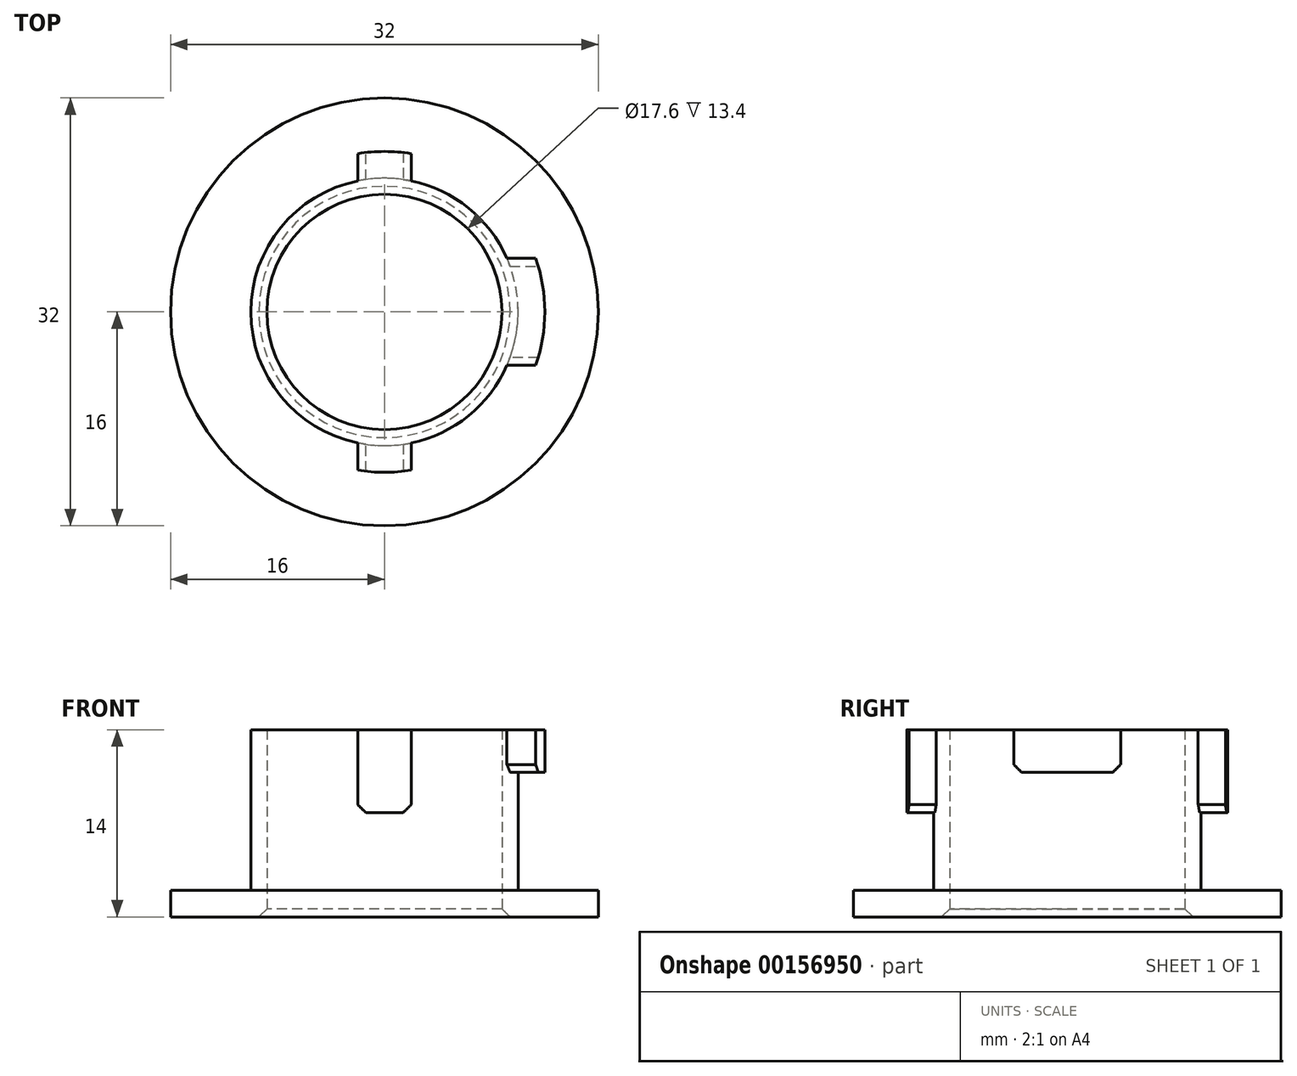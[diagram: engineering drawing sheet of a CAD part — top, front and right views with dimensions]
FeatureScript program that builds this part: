
annotation { "Feature Type Name" : "Feature", "Feature Type Description" : "" }
export const myFeature = defineFeature(function(context is Context, id is Id, definition is map)
    precondition{}
    {
        {
            var Q0;
            Q0=qCreatedBy(makeId("Top.planeOp"),FACE);
            var sketch = newSketch(context, id + "F0", { "sketchPlane" : qUnion([Q0])});
            skCircle(sketch, "E0", {"center": v(0, 0) * mm, "radius": 16 * mm});
            skCircle(sketch, "E1", {"center": v(0, 0) * mm, "radius": 8.8 * mm});
            skSolve(sketch);
        }
        {
            var Q0;
            Q0 = qSketchRegion(id + "F0", true);
            extrude(context, id + "F1", {"entities" : qUnion([Q0]), "depth" : 2 * mm});
        }
        {
            var Q0;
            Q0=makeQuery(id+"F1.opExtrude","CAP_FACE",FACE,{"disambiguationData":[OSD([sQuery(id+"F0.wireOp",EDGE,"E0"),sQuery(id+"F0.wireOp",EDGE,"E1")])],"isStart":false});
            var sketch = newSketch(context, id + "F2", { "sketchPlane" : qUnion([Q0])});
            skCircle(sketch, "E2", {"center": v(0, 0) * mm, "radius": 10 * mm});
            skSolve(sketch);
        }
        {
            var Q0;
            Q0=makeQuery(id+"F2.imprint","IMPRINT",FACE,{"disambiguationData":[TD([[makeQuery(id+"F2.imprint","IMPRINT",EDGE,{"derivedFrom":sQuery(id+"F2.wireOp",EDGE,"E2")}),1.0]])]});
            extrude(context, id + "F3", {"entities" : qUnion([Q0]), "operationType" : NewBodyOperationType.ADD, "depth" : 12 * mm});
        }
        {
            var Q0;
            Q0=makeQuery(id+"F1.opExtrude","CAP_FACE",FACE,{"disambiguationData":[OSD([sQuery(id+"F0.wireOp",EDGE,"E0"),sQuery(id+"F0.wireOp",EDGE,"E1")])],"isStart":false});
            cPlane(context, id + "F4", {"entities" : qUnion([Q0]), "cplaneType" : CPlaneType.OFFSET, "offset" : (3.8 + 2) * mm, "width" : 150 * mm, "height" : 150 * mm});
        }
        {
            var Q0;
            Q0=qCreatedBy(id+"F4.planeOp",FACE);
            var sketch = newSketch(context, id + "F5", { "sketchPlane" : qUnion([Q0])});
            skLineSegment(sketch, "E3", {"start": v(-2, -11.83) * mm, "end": v(-2, -9.8) * mm});
            skArc(sketch, "E4.0", {"start": v(-2, -9.8) * mm, "mid": v(0, -10) * mm, "end": v(2, -9.8) * mm});
            skLineSegment(sketch, "E5.MirrorCS", {"start": v(2, -11.83) * mm, "end": v(2, -9.8) * mm});
            skLineSegment(sketch, "E6.MirrorCS", {"start": v(-2, 11.83) * mm, "end": v(-2, 9.8) * mm});
            skLineSegment(sketch, "E7.MirrorCS", {"start": v(2, 11.83) * mm, "end": v(2, 9.8) * mm});
            skArc(sketch, "E8.trimOffspring", {"start": v(2, 9.8) * mm, "mid": v(0, 10) * mm, "end": v(-2, 9.8) * mm});
            skPoint(sketch, "E9.orphan", {"position": v(12, -4) * mm});
            skPoint(sketch, "E10.MirrorCS.end.orphan", {"position": v(12, 0) * mm});
            skPoint(sketch, "E10.MirrorCS.start.orphan", {"position": v(12, 4) * mm});
            skArc(sketch, "E11.trimOffspring", {"start": v(-2, -11.83) * mm, "mid": v(0, -12) * mm, "end": v(2, -11.83) * mm});
            skPoint(sketch, "E12.end.orphan", {"position": v(0, -12) * mm});
            skPoint(sketch, "E13.MirrorCS.start.orphan", {"position": v(2, -12) * mm});
            skPoint(sketch, "E14.orphan", {"position": v(-2, -12) * mm});
            skArc(sketch, "E15.trimOffspring", {"start": v(2, 11.83) * mm, "mid": v(0, 12) * mm, "end": v(-2, 11.83) * mm});
            skPoint(sketch, "E16.MirrorCS.end.orphan", {"position": v(0, 12) * mm});
            skPoint(sketch, "E16.MirrorCS.start.orphan", {"position": v(-2, 12) * mm});
            skPoint(sketch, "E17.MirrorCS.start.orphan", {"position": v(2, 12) * mm});
            skSolve(sketch);
        }
        {
            var Q0;
            Q0 = qSketchRegion(id + "F5", true);
            var Q1;
            Q1=makeQuery(id+"F3.opExtrude","CAP_FACE",FACE,{"disambiguationData":[OSD([sQuery(id+"F0.wireOp",EDGE,"E1"),sQuery(id+"F2.wireOp",EDGE,"E2")])],"isStart":false});
            extrude(context, id + "F6", {"entities" : qUnion([Q0]), "operationType" : NewBodyOperationType.ADD, "endBound" : BoundingType.UP_TO_SURFACE, "endBoundEntityFace" : qUnion([Q1]), "depth" : 6 * mm});
        }
        {
            var Q0;
            Q0=makeQuery(id+"F2.imprint","IMPRINT",FACE,{"disambiguationData":[TD([[makeQuery(id+"F2.imprint","IMPRINT",EDGE,{"derivedFrom":sQuery(id+"F2.wireOp",EDGE,"E2")}),-1.0]])]});
            cPlane(context, id + "F7", {"entities" : qUnion([Q0]), "cplaneType" : CPlaneType.OFFSET, "offset" : (3.8 + 5) * mm, "width" : 150 * mm, "height" : 150 * mm});
        }
        {
            var Q0;
            Q0=qCreatedBy(id+"F7.planeOp",FACE);
            var sketch = newSketch(context, id + "F8", { "sketchPlane" : qUnion([Q0])});
            skArc(sketch, "E18.0", {"start": v(9.17, -4) * mm, "mid": v(10, 0) * mm, "end": v(9.17, 4) * mm});
            skLineSegment(sketch, "E19", {"start": v(9.17, -4) * mm, "end": v(11.31, -4) * mm});
            skLineSegment(sketch, "E20.MirrorCS", {"start": v(9.17, 4) * mm, "end": v(11.31, 4) * mm});
            skArc(sketch, "E21", {"start": v(11.31, -4) * mm, "mid": v(12, 0) * mm, "end": v(11.31, 4) * mm});
            skPoint(sketch, "E22.end.orphan", {"position": v(12, 0) * mm});
            skPoint(sketch, "E22.start.orphan", {"position": v(12, -4) * mm});
            skPoint(sketch, "E23.orphan", {"position": v(12, 4) * mm});
            skSolve(sketch);
        }
        {
            var Q0;
            Q0 = qSketchRegion(id + "F8", true);
            var Q1;
            {var subQ0=sQuery(id+"F2.wireOp",EDGE,"E2");var subQ1=sQuery(id+"F0.wireOp",EDGE,"E1");Q1=makeQuery(id+"F6.boolean.opBoolean","MERGE",FACE,{"derivedFrom":[makeQuery(id+"F3.opExtrude","CAP_FACE",FACE,{"disambiguationData":[OSD([subQ1,subQ0])],"isStart":false}),makeQuery(id+"F6.opExtrude","CAP_FACE",FACE,{"disambiguationData":[OSD([subQ1,subQ0]),ownerDisambiguation([makeQuery(id+"F6.opExtrude","SWEPT_BODY",BODY,{"disambiguationData":[OSD([sQuery(id+"F5.wireOp",EDGE,"E3"),sQuery(id+"F5.wireOp",EDGE,"E4.0"),sQuery(id+"F5.wireOp",EDGE,"E5.MirrorCS"),sQuery(id+"F5.wireOp",EDGE,"E11.trimOffspring")])]})])],"isStart":false}),makeQuery(id+"F6.opExtrude","CAP_FACE",FACE,{"disambiguationData":[OSD([subQ1,subQ0]),ownerDisambiguation([makeQuery(id+"F6.opExtrude","SWEPT_BODY",BODY,{"disambiguationData":[OSD([sQuery(id+"F5.wireOp",EDGE,"E6.MirrorCS"),sQuery(id+"F5.wireOp",EDGE,"E7.MirrorCS"),sQuery(id+"F5.wireOp",EDGE,"E8.trimOffspring"),sQuery(id+"F5.wireOp",EDGE,"E15.trimOffspring")])]})])],"isStart":false})]});}
            extrude(context, id + "F9", {"entities" : qUnion([Q0]), "operationType" : NewBodyOperationType.ADD, "endBound" : BoundingType.UP_TO_SURFACE, "endBoundEntityFace" : qUnion([Q1]), "depth" : 3 * mm});
        }
        {
            var Q0;
            Q0=makeQuery(id+"F1.opExtrude","CAP_EDGE",EDGE,{"disambiguationData":[OSD([sQuery(id+"F0.wireOp",EDGE,"E1")])],"isStart":true});
            var Q1;
            Q1=makeQuery(id+"F6.opExtrude","CAP_EDGE",EDGE,{"disambiguationData":[OSD([sQuery(id+"F5.wireOp",EDGE,"E6.MirrorCS")])],"isStart":true});
            var Q2;
            Q2=makeQuery(id+"F6.opExtrude","CAP_EDGE",EDGE,{"disambiguationData":[OSD([sQuery(id+"F5.wireOp",EDGE,"E7.MirrorCS")])],"isStart":true});
            var Q3;
            Q3=makeQuery(id+"F9.opExtrude","CAP_EDGE",EDGE,{"disambiguationData":[OSD([sQuery(id+"F8.wireOp",EDGE,"E20.MirrorCS")])],"isStart":true});
            var Q4;
            Q4=makeQuery(id+"F9.opExtrude","CAP_EDGE",EDGE,{"disambiguationData":[OSD([sQuery(id+"F8.wireOp",EDGE,"E19")])],"isStart":true});
            var Q5;
            Q5=makeQuery(id+"F6.opExtrude","CAP_EDGE",EDGE,{"disambiguationData":[OSD([sQuery(id+"F5.wireOp",EDGE,"E3")])],"isStart":true});
            var Q6;
            Q6=makeQuery(id+"F6.opExtrude","CAP_EDGE",EDGE,{"disambiguationData":[OSD([sQuery(id+"F5.wireOp",EDGE,"E5.MirrorCS")])],"isStart":true});
            chamfer(context, id + "F10", {"entities" : qUnion([Q0, Q1, Q2, Q3, Q4, Q5, Q6]), "width" : 0.6 * mm, "tangentPropagation" : true});
        }
    });
